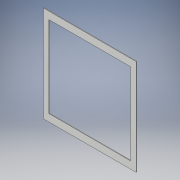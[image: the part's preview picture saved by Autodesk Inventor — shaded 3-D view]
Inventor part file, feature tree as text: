
AUTODESK INVENTOR PART (.ipt)
format: ipt  version: 2017 (Build 210142000, 142)  size: 107,520 bytes
history: native  units: in
note: dims shown in document units (in); Inventor stores cm internally (conversion verified against a paired STEP export)
features: extrude x2, sketch x2
ambient origin geometry x8: Origin, YZ Plane, XZ Plane, XY Plane, X Axis, Y Axis, Z Axis, Center Point
bodies: Solid1 (feature_tree)
feature tree (4):
  extrude  "Extrusion1"  Depth=20.0in
  extrude  "Extrusion2"  Depth=17.0in
  sketch  "Sketch1"  dims[d0=19.333in d1=20.0in]
  sketch  "Sketch2"  dims[d2=0.125in d3=0.0in d4=17.0in d5=17.0in d6=0.125in d7=0.0in]
